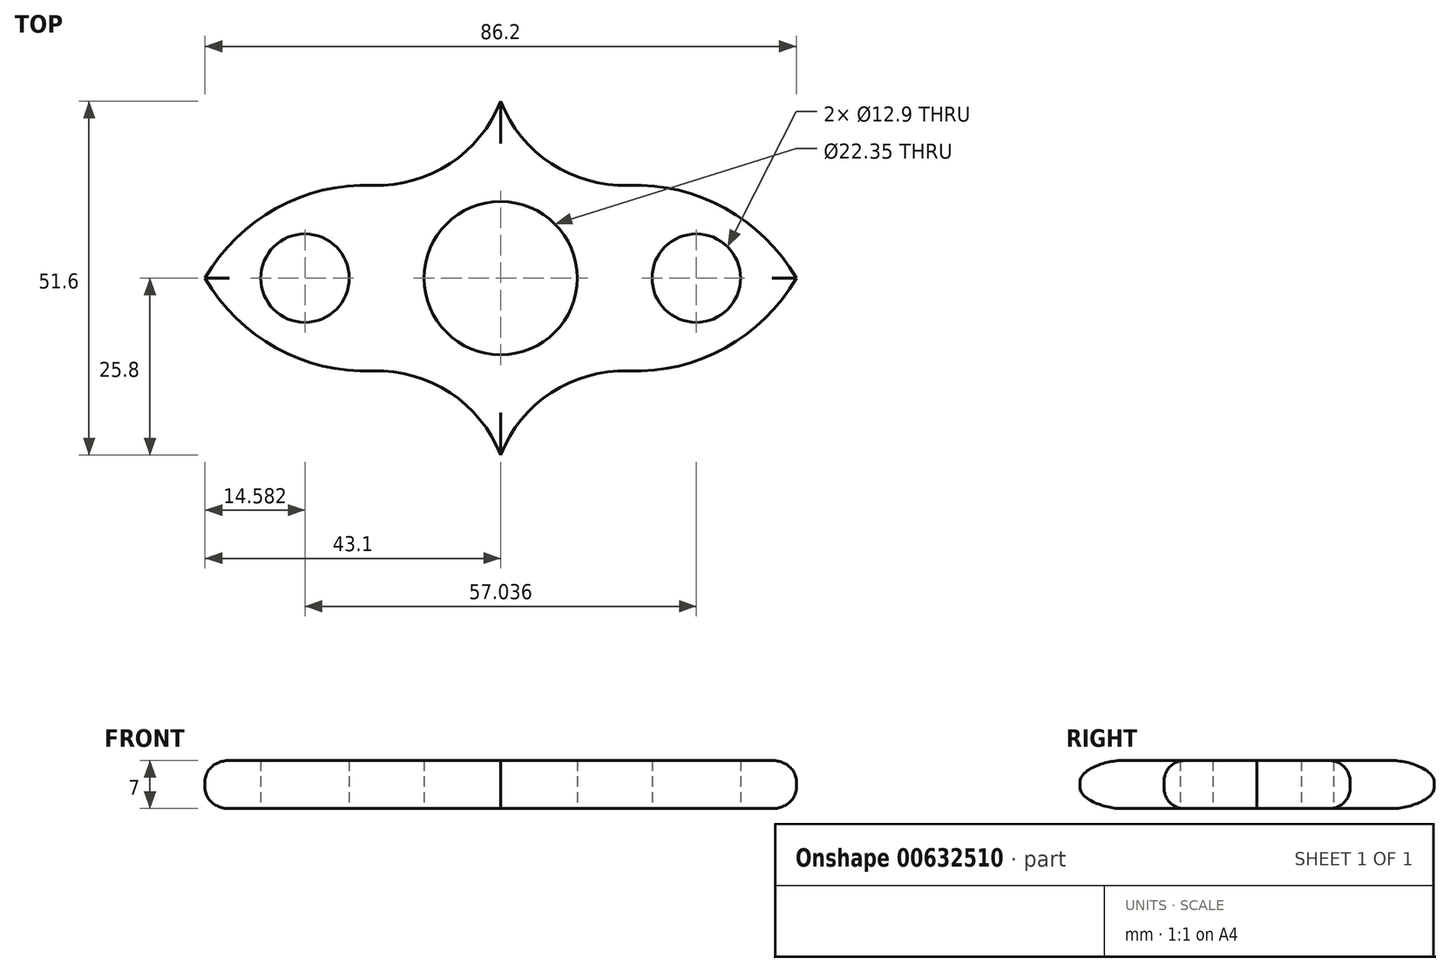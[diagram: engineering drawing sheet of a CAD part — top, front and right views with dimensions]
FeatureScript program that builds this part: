
annotation { "Feature Type Name" : "Feature", "Feature Type Description" : "" }
export const myFeature = defineFeature(function(context is Context, id is Id, definition is map)
    precondition{}
    {
        {
            var Q0;
            Q0=qCreatedBy(makeId("Top.planeOp"),FACE);
            var sketch = newSketch(context, id + "F0", { "sketchPlane" : qUnion([Q0])});
            skCircle(sketch, "E0", {"center": v(0, 0) * mm, "radius": 11.18 * mm});
            skCircle(sketch, "E1", {"center": v(0, 0) * mm, "radius": 15.1 * mm});
            skArc(sketch, "E2", {"start": v(43.1, 0) * mm, "mid": v(28.52, 12.05) * mm, "end": v(9.6, 11.66) * mm});
            skArc(sketch, "E3.MirrorCS", {"start": v(43.1, 0) * mm, "mid": v(28.52, -12.05) * mm, "end": v(9.6, -11.66) * mm});
            skArc(sketch, "E4.MirrorCS", {"start": v(-43.1, 0) * mm, "mid": v(-28.52, 12.05) * mm, "end": v(-9.6, 11.66) * mm});
            skArc(sketch, "E5.MirrorCS", {"start": v(-43.1, 0) * mm, "mid": v(-28.52, -12.05) * mm, "end": v(-9.6, -11.66) * mm});
            skArc(sketch, "E6", {"start": v(-19.59, 13.6) * mm, "mid": v(-7.77, 16.44) * mm, "end": v(0, 25.8) * mm});
            skArc(sketch, "E7.MirrorCS", {"start": v(19.59, 13.6) * mm, "mid": v(7.77, 16.44) * mm, "end": v(0, 25.8) * mm});
            skArc(sketch, "E8.MirrorCS", {"start": v(-19.59, -13.6) * mm, "mid": v(-7.77, -16.44) * mm, "end": v(0, -25.8) * mm});
            skArc(sketch, "E9.MirrorCS", {"start": v(19.59, -13.6) * mm, "mid": v(7.77, -16.44) * mm, "end": v(0, -25.8) * mm});
            skCircle(sketch, "E10", {"center": v(-28.52, 0) * mm, "radius": 6.45 * mm});
            skPoint(sketch, "E10.centerSnap0", {"position": v(-28.52, -12.05) * mm});
            skCircle(sketch, "E11.MirrorC", {"center": v(28.52, 0) * mm, "radius": 6.45 * mm});
            skSolve(sketch);
        }
        {
            var Q0;
            Q0 = qSketchRegion(id + "F0", true);
            var Q1;
            Q1=makeQuery(id+"F0.imprint","IMPRINT",FACE,{"disambiguationData":[TD([[makeQuery(id+"F0.imprint","IMPRINT",EDGE,{"derivedFrom":sQuery(id+"F0.wireOp",EDGE,"E0")}),-1.0]])]});
            extrude(context, id + "F1", {"entities" : qUnion([Q0, Q1]), "depth" : 7 * mm, "offsetDistance" : 25 * mm});
        }
        {
            var Q0;
            Q0=makeQuery(id+"F1.opExtrude","CAP_EDGE",EDGE,{"disambiguationData":[OSD([sQuery(id+"F0.wireOp",EDGE,"E9.MirrorCS")])],"isStart":false});
            var Q1;
            Q1=makeQuery(id+"F1.opExtrude","CAP_EDGE",EDGE,{"disambiguationData":[OSD([sQuery(id+"F0.wireOp",EDGE,"E3.MirrorCS")])],"isStart":false});
            var Q2;
            Q2=makeQuery(id+"F1.opExtrude","CAP_EDGE",EDGE,{"disambiguationData":[OSD([sQuery(id+"F0.wireOp",EDGE,"E2")])],"isStart":false});
            var Q3;
            Q3=makeQuery(id+"F1.opExtrude","CAP_EDGE",EDGE,{"disambiguationData":[OSD([sQuery(id+"F0.wireOp",EDGE,"E7.MirrorCS")])],"isStart":false});
            var Q4;
            Q4=makeQuery(id+"F1.opExtrude","CAP_EDGE",EDGE,{"disambiguationData":[OSD([sQuery(id+"F0.wireOp",EDGE,"E6")])],"isStart":false});
            var Q5;
            Q5=makeQuery(id+"F1.opExtrude","CAP_EDGE",EDGE,{"disambiguationData":[OSD([sQuery(id+"F0.wireOp",EDGE,"E5.MirrorCS")])],"isStart":false});
            var Q6;
            Q6=makeQuery(id+"F1.opExtrude","CAP_EDGE",EDGE,{"disambiguationData":[OSD([sQuery(id+"F0.wireOp",EDGE,"E8.MirrorCS")])],"isStart":false});
            var Q7;
            Q7=makeQuery(id+"F1.opExtrude","CAP_EDGE",EDGE,{"disambiguationData":[OSD([sQuery(id+"F0.wireOp",EDGE,"E4.MirrorCS")])],"isStart":false});
            var Q8;
            Q8=makeQuery(id+"F1.opExtrude","CAP_EDGE",EDGE,{"disambiguationData":[OSD([sQuery(id+"F0.wireOp",EDGE,"E9.MirrorCS")])],"isStart":true});
            var Q9;
            Q9=makeQuery(id+"F1.opExtrude","CAP_EDGE",EDGE,{"disambiguationData":[OSD([sQuery(id+"F0.wireOp",EDGE,"E3.MirrorCS")])],"isStart":true});
            var Q10;
            Q10=makeQuery(id+"F1.opExtrude","CAP_EDGE",EDGE,{"disambiguationData":[OSD([sQuery(id+"F0.wireOp",EDGE,"E8.MirrorCS")])],"isStart":true});
            var Q11;
            Q11=makeQuery(id+"F1.opExtrude","CAP_EDGE",EDGE,{"disambiguationData":[OSD([sQuery(id+"F0.wireOp",EDGE,"E5.MirrorCS")])],"isStart":true});
            var Q12;
            Q12=makeQuery(id+"F1.opExtrude","CAP_EDGE",EDGE,{"disambiguationData":[OSD([sQuery(id+"F0.wireOp",EDGE,"E4.MirrorCS")])],"isStart":true});
            var Q13;
            Q13=makeQuery(id+"F1.opExtrude","CAP_EDGE",EDGE,{"disambiguationData":[OSD([sQuery(id+"F0.wireOp",EDGE,"E6")])],"isStart":true});
            var Q14;
            Q14=makeQuery(id+"F1.opExtrude","CAP_EDGE",EDGE,{"disambiguationData":[OSD([sQuery(id+"F0.wireOp",EDGE,"E7.MirrorCS")])],"isStart":true});
            var Q15;
            Q15=makeQuery(id+"F1.opExtrude","CAP_EDGE",EDGE,{"disambiguationData":[OSD([sQuery(id+"F0.wireOp",EDGE,"E2")])],"isStart":true});
            fillet(context, id + "F2", {"entities" : qUnion([Q0, Q1, Q2, Q3, Q4, Q5, Q6, Q7, Q8, Q9, Q10, Q11, Q12, Q13, Q14, Q15]), "radius" : 3 * mm, "tangentPropagation" : true, "allowEdgeOverflow" : false});
        }
    });
